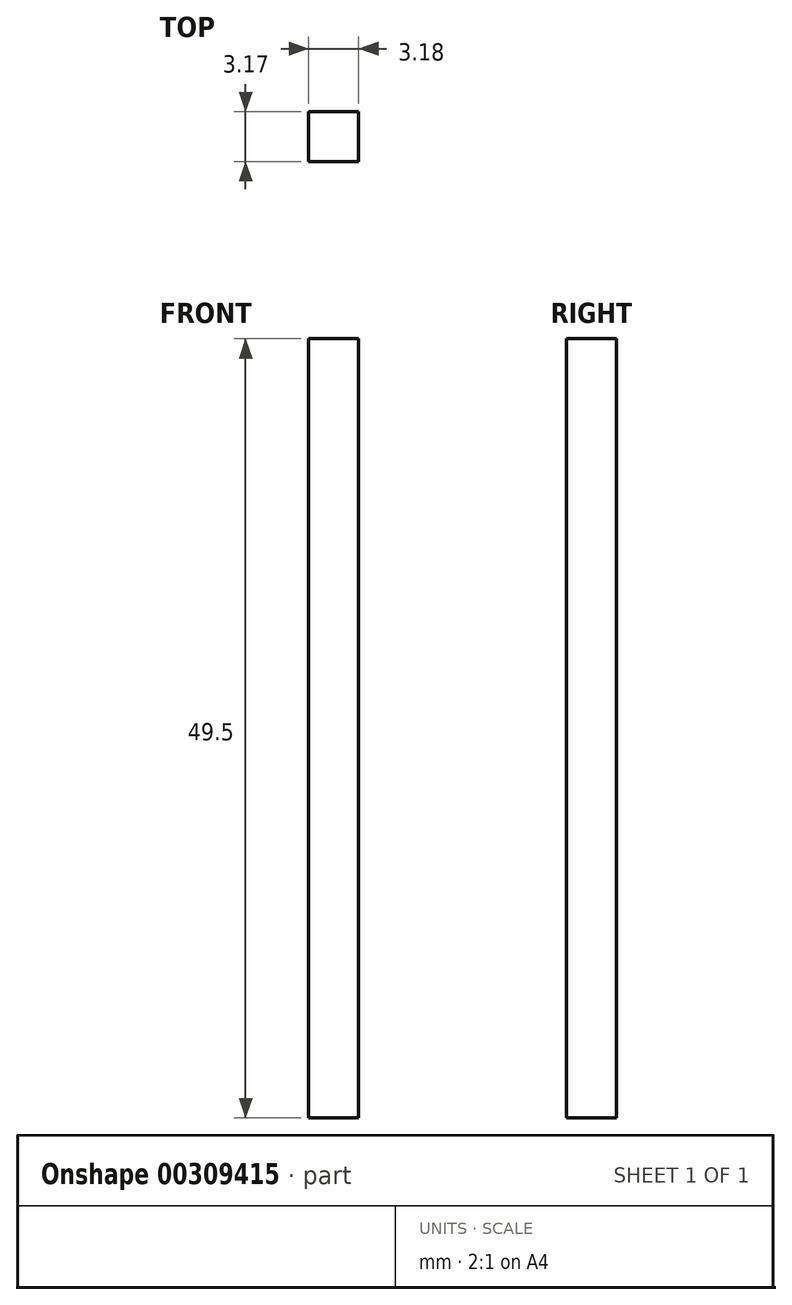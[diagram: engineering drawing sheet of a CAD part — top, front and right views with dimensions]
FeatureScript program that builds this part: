
annotation { "Feature Type Name" : "Feature", "Feature Type Description" : "" }
export const myFeature = defineFeature(function(context is Context, id is Id, definition is map)
    precondition{}
    {
        {
            var Q0;
            Q0=qCreatedBy(makeId("Front.planeOp"),FACE);
            var sketch = newSketch(context, id + "F0", { "sketchPlane" : qUnion([Q0])});
            skLineSegment(sketch, "E0.bottom", {"start": v(1.59, 24.75) * mm, "end": v(-1.59, 24.75) * mm});
            skLineSegment(sketch, "E0.top", {"start": v(1.59, -24.75) * mm, "end": v(-1.59, -24.75) * mm});
            skLineSegment(sketch, "E0.left", {"start": v(1.59, 24.75) * mm, "end": v(1.59, -24.75) * mm});
            skLineSegment(sketch, "E0.right", {"start": v(-1.59, 24.75) * mm, "end": v(-1.59, -24.75) * mm});
            skPoint(sketch, "E0.middle", {"position": v(0, 0) * mm});
            skSolve(sketch);
        }
        {
            var Q0;
            Q0=makeQuery(id+"F0.imprint","IMPRINT",FACE,{"disambiguationData":[TD([[makeQuery(id+"F0.imprint","IMPRINT",EDGE,{"derivedFrom":sQuery(id+"F0.wireOp",EDGE,"E0.bottom")}),1.0]])]});
            extrude(context, id + "F1", {"entities" : qUnion([Q0]), "depth" : 3.17 * mm});
        }
    });
